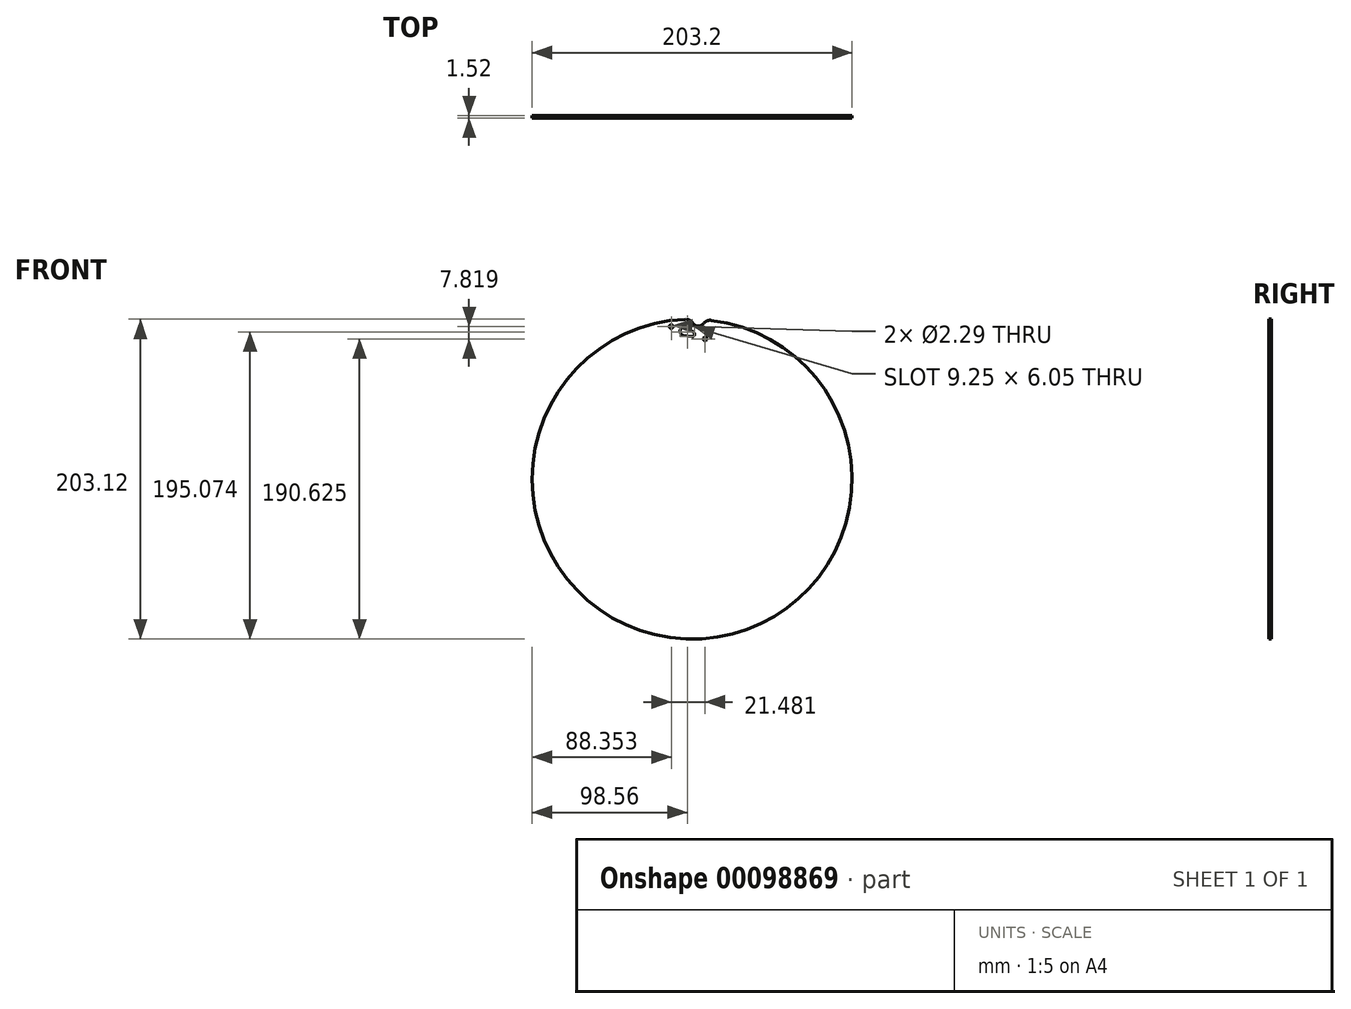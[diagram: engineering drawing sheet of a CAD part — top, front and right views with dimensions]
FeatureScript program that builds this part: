
annotation { "Feature Type Name" : "Feature", "Feature Type Description" : "" }
export const myFeature = defineFeature(function(context is Context, id is Id, definition is map)
    precondition{}
    {
        {
            var Q0;
            Q0=qCreatedBy(makeId("Front.planeOp"),FACE);
            var sketch = newSketch(context, id + "F0", { "sketchPlane" : qUnion([Q0])});
            skCircle(sketch, "E0", {"center": v(0, 0) * mm, "radius": 101.6 * mm});
            skSolve(sketch);
        }
        {
            var Q0;
            Q0 = qSketchRegion(id + "F0", true);
            extrude(context, id + "F1", {"entities" : qUnion([Q0]), "depth" : 1.52 * mm});
        }
        {
            var Q0;
            Q0=makeQuery(id+"F1.opExtrude","CAP_FACE",FACE,{"disambiguationData":[OSD([sQuery(id+"F0.wireOp",EDGE,"E0")])],"isStart":true});
            var sketch = newSketch(context, id + "F2", { "sketchPlane" : qUnion([Q0])});
            skCircle(sketch, "E1", {"center": v(5.01, 93.85) * mm, "radius": 2.67 * mm});
            skCircle(sketch, "E2", {"center": v(0, 92.02) * mm, "radius": 1.59 * mm});
            skLineSegment(sketch, "E3", {"start": v(5.4, 91.2) * mm, "end": v(0.23, 90.45) * mm});
            skLineSegment(sketch, "E4", {"start": v(3.61, 96.12) * mm, "end": v(-0.83, 93.37) * mm});
            skLineSegment(sketch, "E5", {"start": v(5.01, 93.85) * mm, "end": v(0, 92.02) * mm});
            skLineSegment(sketch, "E6", {"start": v(0, 0) * mm, "end": v(0, 92.02) * mm});
            skSolve(sketch);
        }
        {
            var Q0;
            Q0 = qSketchRegion(id + "F2", true);
            extrude(context, id + "F3", {"entities" : qUnion([Q0]), "operationType" : NewBodyOperationType.REMOVE, "endBound" : BoundingType.THROUGH_ALL, "oppositeDirection" : true, "depth" : 25.4 * mm});
        }
        {
            var Q0;
            Q0=makeQuery(id+"F1.opExtrude","CAP_FACE",FACE,{"disambiguationData":[OSD([sQuery(id+"F0.wireOp",EDGE,"E0")])],"isStart":true});
            var sketch = newSketch(context, id + "F4", { "sketchPlane" : qUnion([Q0])});
            skLineSegment(sketch, "E7", {"start": v(-8.23, 89.02) * mm, "end": v(13.25, 96.84) * mm});
            skCircle(sketch, "E8", {"center": v(-8.23, 89.02) * mm, "radius": 1.14 * mm});
            skCircle(sketch, "E9", {"center": v(13.25, 96.84) * mm, "radius": 1.14 * mm});
            skCircle(sketch, "E10", {"center": v(-3.97, 101.52) * mm, "radius": 4.32 * mm});
            skLineSegment(sketch, "E11", {"start": v(-3.97, 101.52) * mm, "end": v(-3.65, 93.5) * mm});
            skLineSegment(sketch, "E12", {"start": v(5.01, 93.85) * mm, "end": v(-12.32, 93.17) * mm});
            skSolve(sketch);
        }
        {
            var Q0;
            Q0 = qSketchRegion(id + "F4", true);
            extrude(context, id + "F5", {"entities" : qUnion([Q0]), "operationType" : NewBodyOperationType.REMOVE, "endBound" : BoundingType.THROUGH_ALL, "oppositeDirection" : true, "depth" : 25.4 * mm});
        }
        {
            var Q0;
            Q0=makeQuery(id+"F5.boolean.opBoolean","INTERSECT",EDGE,{"disambiguationData":[OD(1.0)],"derivedFrom":[makeQuery(id+"F1.opExtrude","SWEPT_FACE",FACE,{"disambiguationData":[OSD([sQuery(id+"F0.wireOp",EDGE,"E0")])]}),makeQuery(id+"F5.opExtrude","SWEPT_FACE",FACE,{"disambiguationData":[OSD([sQuery(id+"F4.wireOp",EDGE,"E10")])]})]});
            var Q1;
            Q1=makeQuery(id+"F5.boolean.opBoolean","INTERSECT",EDGE,{"disambiguationData":[OD(0.0)],"derivedFrom":[makeQuery(id+"F1.opExtrude","SWEPT_FACE",FACE,{"disambiguationData":[OSD([sQuery(id+"F0.wireOp",EDGE,"E0")])]}),makeQuery(id+"F5.opExtrude","SWEPT_FACE",FACE,{"disambiguationData":[OSD([sQuery(id+"F4.wireOp",EDGE,"E10")])]})]});
            fillet(context, id + "F6", {"entities" : qUnion([Q0, Q1]), "radius" : 5.08 * mm, "tangentPropagation" : true, "allowEdgeOverflow" : false});
        }
    });
